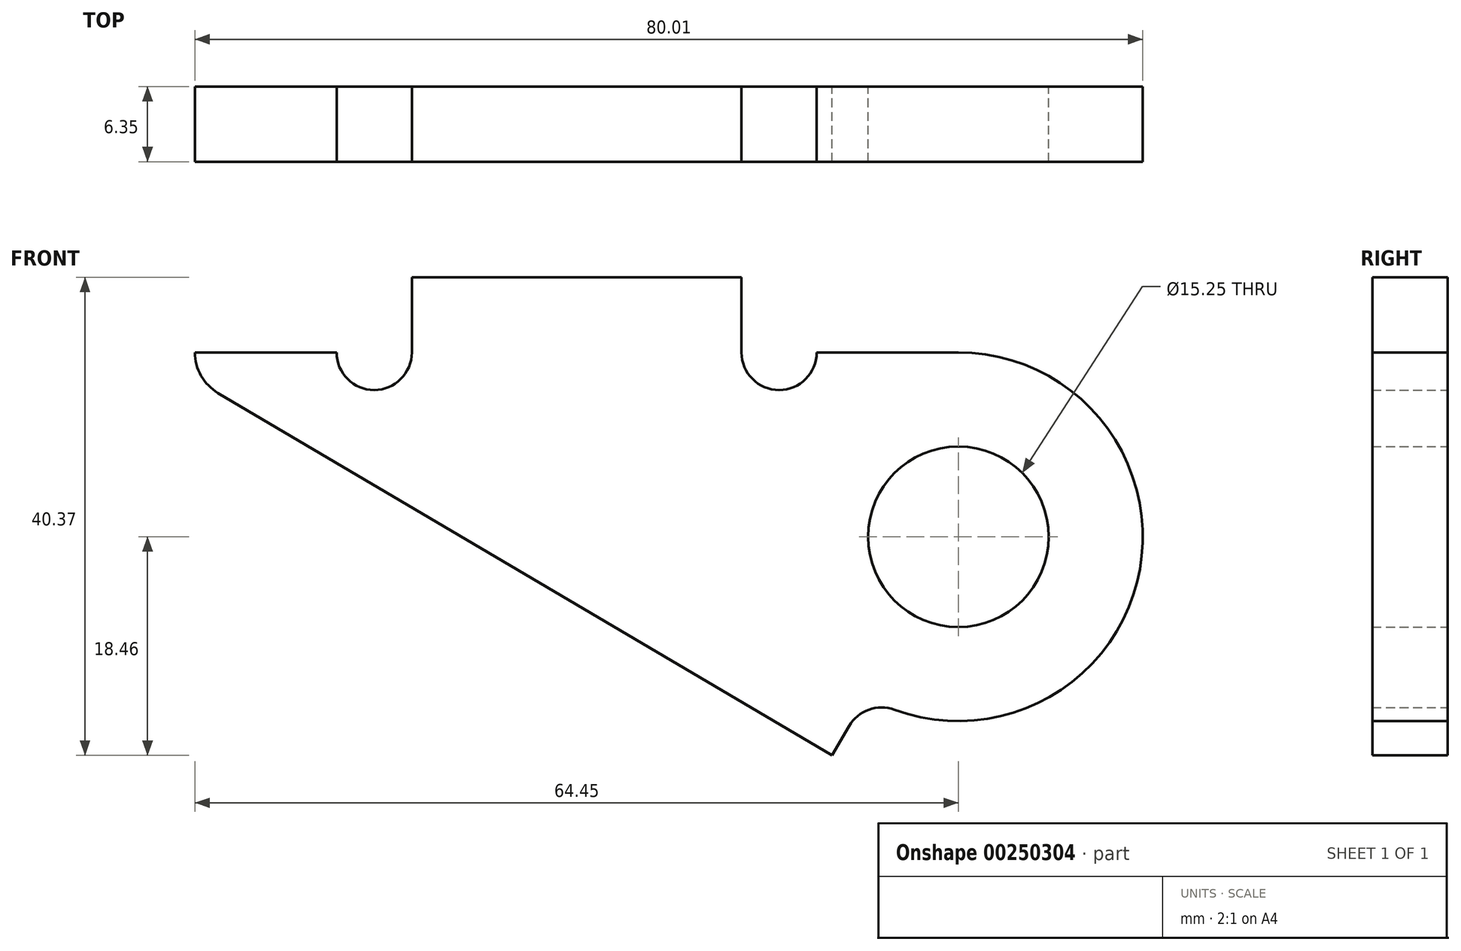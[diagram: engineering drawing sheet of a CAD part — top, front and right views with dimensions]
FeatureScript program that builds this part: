
annotation { "Feature Type Name" : "Feature", "Feature Type Description" : "" }
export const myFeature = defineFeature(function(context is Context, id is Id, definition is map)
    precondition{}
    {
        {
            var Q0;
            Q0=qCreatedBy(makeId("Front.planeOp"),FACE);
            var sketch = newSketch(context, id + "F0", { "sketchPlane" : qUnion([Q0])});
            skLineSegment(sketch, "E0", {"start": v(-46.14, 21.91) * mm, "end": v(-18.3, 21.91) * mm});
            skLineSegment(sketch, "E1", {"start": v(-46.14, 15.56) * mm, "end": v(-46.14, 21.91) * mm});
            skArc(sketch, "E2", {"start": v(-52.5, 15.56) * mm, "mid": v(-49.32, 12.39) * mm, "end": v(-46.14, 15.56) * mm});
            skLineSegment(sketch, "E3", {"start": v(-64.45, 15.56) * mm, "end": v(-52.5, 15.56) * mm});
            skArc(sketch, "E4", {"start": v(-64.45, 15.56) * mm, "mid": v(-63.93, 13.6) * mm, "end": v(-62.5, 12.14) * mm});
            skLineSegment(sketch, "E5", {"start": v(-10.66, -18.46) * mm, "end": v(-62.5, 12.14) * mm});
            skLineSegment(sketch, "E6", {"start": v(-9.23, -16) * mm, "end": v(-10.66, -18.46) * mm});
            skArc(sketch, "E7", {"start": v(-5.39, -14.6) * mm, "mid": v(-7.56, -14.6) * mm, "end": v(-9.23, -16) * mm});
            skArc(sketch, "E8", {"start": v(-5.39, -14.6) * mm, "mid": v(15.32, -2.74) * mm, "end": v(0, 15.56) * mm});
            skLineSegment(sketch, "E9", {"start": v(-11.96, 15.56) * mm, "end": v(0, 15.56) * mm});
            skArc(sketch, "E10", {"start": v(-18.3, 15.56) * mm, "mid": v(-15.13, 12.39) * mm, "end": v(-11.96, 15.56) * mm});
            skLineSegment(sketch, "E11", {"start": v(-18.3, 21.91) * mm, "end": v(-18.3, 15.56) * mm});
            skArc(sketch, "E12", {"start": v(-13.82, 7.82) * mm, "mid": v(-15.61, -2.88) * mm, "end": v(-10.12, -12.23) * mm});
            skCircle(sketch, "E13", {"center": v(0, 0) * mm, "radius": 7.63 * mm});
            skArc(sketch, "E14", {"start": v(-13.82, 7.82) * mm, "mid": v(-13.67, 10.66) * mm, "end": v(-15.86, 12.47) * mm});
            skArc(sketch, "E15", {"start": v(-9.4, -16.27) * mm, "mid": v(-9.02, -14.12) * mm, "end": v(-10.12, -12.23) * mm});
            skSolve(sketch);
        }
        {
            var Q0;
            {var subQ1=sQuery(id+"F0.wireOp",EDGE,"E7");Q0=makeQuery(id+"F0.imprint","IMPRINT",FACE,{"disambiguationData":[TD([[makeQuery(id+"F0.imprint","IMPRINT",EDGE,{"derivedFrom":subQ1}),-1.0]])]});}
            extrude(context, id + "F1", {"entities" : qUnion([Q0]), "depth" : 3.17 * mm});
        }
        {
            var Q0;
            Q0=makeQuery(id+"F0.imprint","IMPRINT",FACE,{"disambiguationData":[TD([[makeQuery(id+"F0.imprint","IMPRINT",EDGE,{"derivedFrom":sQuery(id+"F0.wireOp",EDGE,"E0")}),-1.0]])]});
            extrude(context, id + "F2", {"entities" : qUnion([Q0]), "operationType" : NewBodyOperationType.ADD, "depth" : 6.35 * mm});
        }
    });
